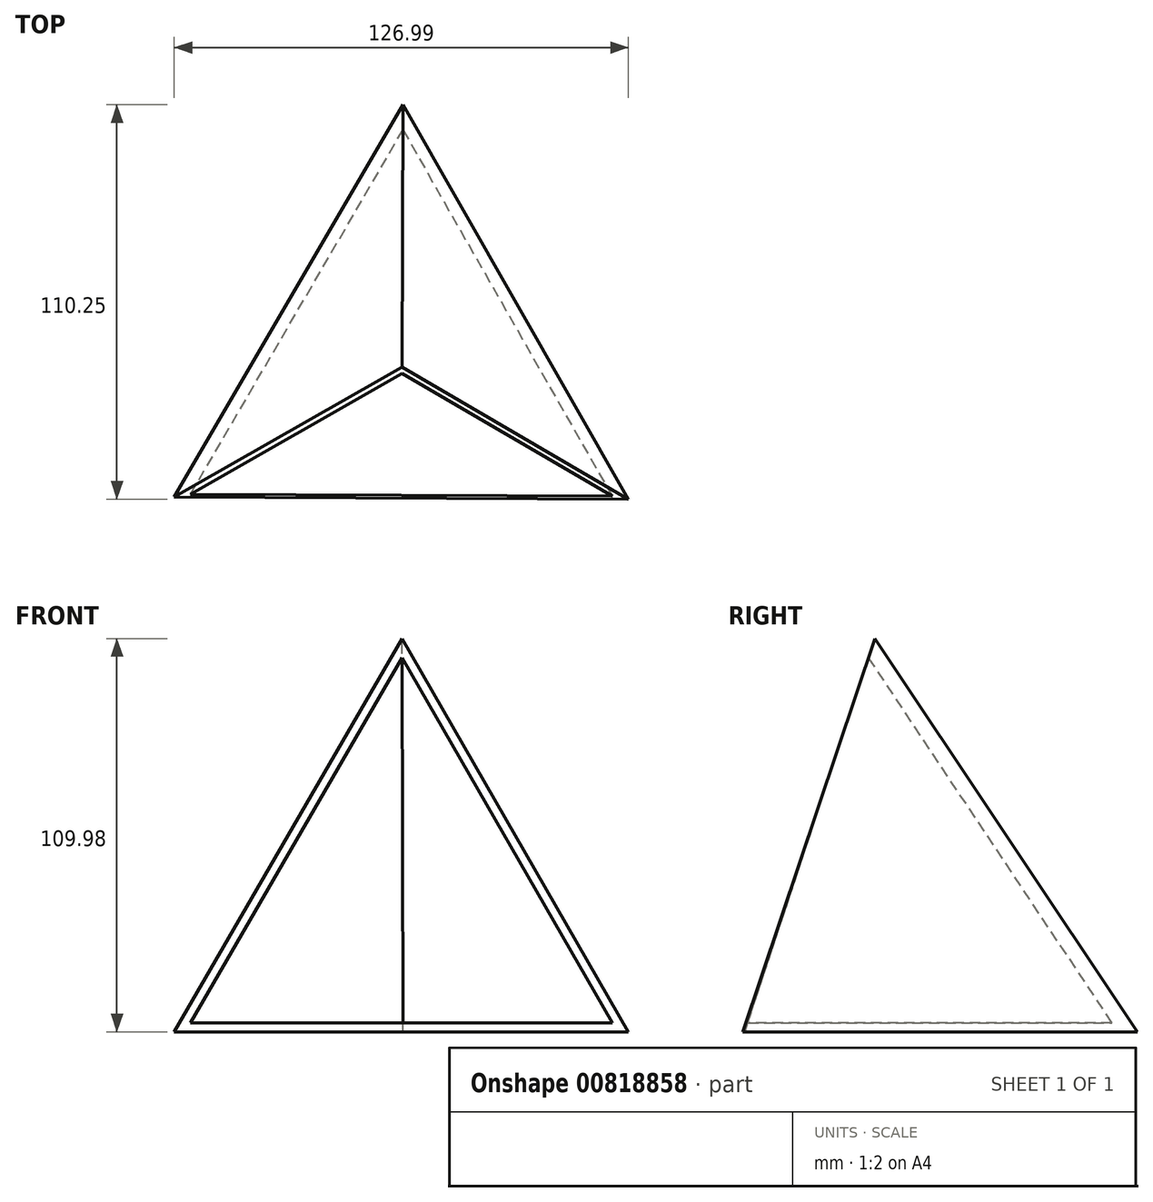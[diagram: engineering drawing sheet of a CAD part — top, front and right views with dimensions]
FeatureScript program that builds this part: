
annotation { "Feature Type Name" : "Feature", "Feature Type Description" : "" }
export const myFeature = defineFeature(function(context is Context, id is Id, definition is map)
    precondition{}
    {
        {
            var Q0;
            Q0=qCreatedBy(makeId("Top.planeOp"),FACE);
            var sketch = newSketch(context, id + "F0", { "sketchPlane" : qUnion([Q0])});
            skCircle(sketch, "E0.cCircle", {"center": v(0, 0) * mm, "radius": 36.66 * mm, "construction": true});
            skLineSegment(sketch, "E0.0", {"start": v(0.31, 73.32) * mm, "end": v(63.34, -36.93) * mm});
            skLineSegment(sketch, "E0.1", {"start": v(63.34, -36.93) * mm, "end": v(-63.65, -36.4) * mm});
            skLineSegment(sketch, "E0.2", {"start": v(-63.65, -36.4) * mm, "end": v(0.31, 73.32) * mm});
            skPoint(sketch, "E0.0.midPoint", {"position": v(31.83, 18.2) * mm});
            skSolve(sketch);
        }
        {
            var Q0;
            Q0=qCreatedBy(makeId("Front.planeOp"),FACE);
            var sketch = newSketch(context, id + "F1", { "sketchPlane" : qUnion([Q0])});
            skPoint(sketch, "E1", {"position": v(0, 109.98) * mm});
            skSolve(sketch);
        }
        {
            var Q0;
            Q0=makeQuery(id+"F0.imprint","IMPRINT",FACE,{"disambiguationData":[TD([[makeQuery(id+"F0.imprint","IMPRINT",EDGE,{"derivedFrom":sQuery(id+"F0.wireOp",EDGE,"E0.0")}),-1.0]])]});
            var Q1;
            Q1=sQuery(id+"F1.wireOp",VERTEX,"E1");
            loft(context, id + "F2", {"sheetProfilesArray" : [{ "sheetProfileEntities" : qUnion([Q0]) }, { "sheetProfileEntities" : qUnion([Q1]) }]});
        }
        {
            var Q0;
            {var subQ0=sQuery(id+"F0.wireOp",EDGE,"E0.1");var subQ1=sQuery(id+"F0.wireOp",EDGE,"E0.2");var subQ2=sQuery(id+"F0.wireOp",EDGE,"E0.0");Q0=makeQuery(id+"F2.opLoft","SWEPT_FACE",FACE,{"disambiguationData":[OSD([subQ2,subQ0,subQ1]),TDD([makeQuery(id+"F0.imprint","INTERSECT",VERTEX,{"derivedFrom":[subQ2,subQ0]}),makeQuery(id+"F0.imprint","INTERSECT",VERTEX,{"derivedFrom":[subQ0,subQ1]}),makeQuery(id+"F0.imprint","IMPRINT",EDGE,{"derivedFrom":subQ0})])]});}
            shell(context, id + "F3", {"entities" : qUnion([Q0]), "thickness" : 2.54 * mm});
        }
    });
